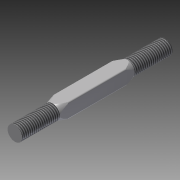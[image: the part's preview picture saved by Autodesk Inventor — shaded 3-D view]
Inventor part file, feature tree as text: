
AUTODESK INVENTOR PART (.ipt)
format: ipt  version: 2013 (Build 170138000, 138)  size: 145,920 bytes
history: native  units: mm
features: sketch x3, extrude x2, thread x2, other x1, plane x1, revolve x1, fillet x1
ambient origin geometry x8: Origin, YZ Plane, XZ Plane, XY Plane, X Axis, Y Axis, Z Axis, Center Point
feature tree (11):
  other  "Sólido1"
  extrude  "Extrusión1"  Depth=72.0mm TaperAngle=0.0deg
  plane  "Plano de trabajo1"
  extrude  "Extrusión3"  Depth=36.0mm TaperAngle=0.0deg
  revolve  "Revolución2"  [1 undecoded]
  fillet  "Empalme1"  Radius=7.0mm
  thread  "Rosca1"  [1 undecoded]
  thread  "Rosca2"  [1 undecoded]
  sketch  "Boceto1"  dims[d0=7.0mm d1=72.0mm d2=0.0mm]
  sketch  "Boceto3"  dims[d13=18.0mm d18=36.0mm d19=0.0mm]
  sketch  "Boceto4"  dims[d26=3.5mm d27=3.5mm d28=7.0mm d29=7.0mm d31=18.0mm d32=3.5mm d36=3.5mm d39=90.0deg d40=0.5mm d41=10.0mm d42=0.0mm d43=10.0mm d44=0.0mm]
note: 3 required parameter values undecoded (feature->parameter linkage not recoverable at this tier; creation-order binding heuristic only, values carry confidence <= 0.55)